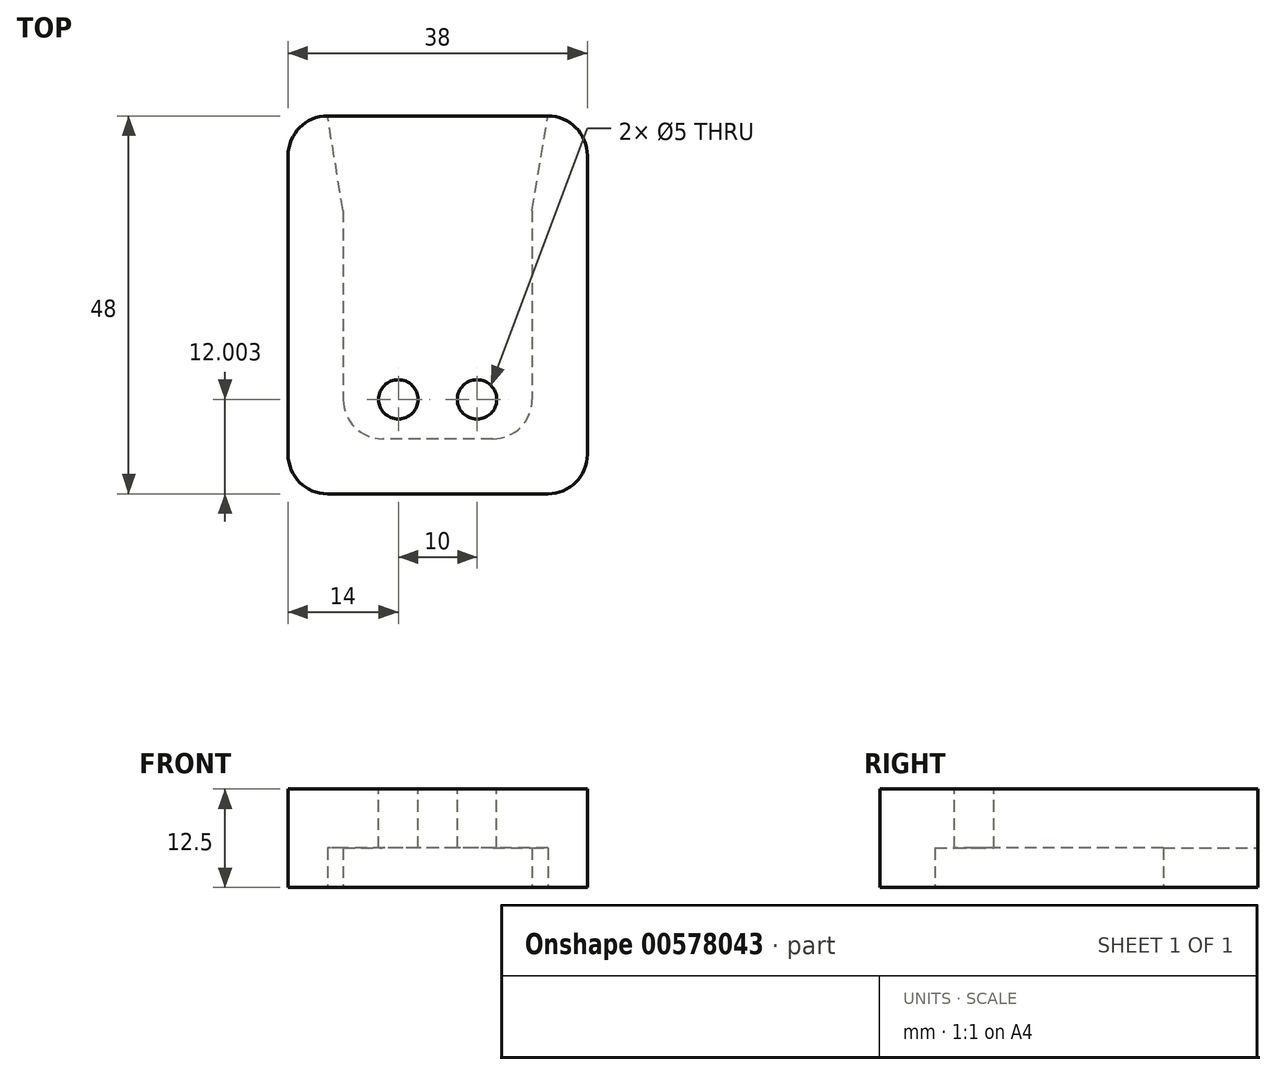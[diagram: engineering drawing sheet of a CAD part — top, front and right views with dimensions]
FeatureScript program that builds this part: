
annotation { "Feature Type Name" : "Feature", "Feature Type Description" : "" }
export const myFeature = defineFeature(function(context is Context, id is Id, definition is map)
    precondition{}
    {
        {
            var Q0;
            Q0=qCreatedBy(makeId("Top.planeOp"),FACE);
            var sketch = newSketch(context, id + "F0", { "sketchPlane" : qUnion([Q0])});
            skLineSegment(sketch, "E0.bottom", {"start": v(19, 24.01) * mm, "end": v(-19, 24.01) * mm});
            skLineSegment(sketch, "E0.top", {"start": v(19, -23.99) * mm, "end": v(-19, -23.99) * mm});
            skLineSegment(sketch, "E0.left", {"start": v(19, 24.01) * mm, "end": v(19, -23.99) * mm});
            skLineSegment(sketch, "E0.right", {"start": v(-19, 24.01) * mm, "end": v(-19, -23.99) * mm});
            skPoint(sketch, "E0.middle", {"position": v(0, 0.01) * mm});
            skLineSegment(sketch, "E1.bottom", {"start": v(12, 17.01) * mm, "end": v(-12, 17.01) * mm});
            skLineSegment(sketch, "E1.top", {"start": v(12, -16.99) * mm, "end": v(-12, -16.99) * mm});
            skLineSegment(sketch, "E1.left", {"start": v(12, 17.01) * mm, "end": v(12, -16.99) * mm});
            skLineSegment(sketch, "E1.right", {"start": v(-12, 17.01) * mm, "end": v(-12, -16.99) * mm});
            skSolve(sketch);
        }
        {
            var Q0;
            Q0=makeQuery(id+"F0.imprint","IMPRINT",FACE,{"disambiguationData":[TD([[makeQuery(id+"F0.imprint","IMPRINT",EDGE,{"derivedFrom":sQuery(id+"F0.wireOp",EDGE,"E0.bottom")}),1.0]])]});
            var Q1;
            Q1=makeQuery(id+"F0.imprint","IMPRINT",FACE,{"disambiguationData":[TD([[makeQuery(id+"F0.imprint","IMPRINT",EDGE,{"derivedFrom":sQuery(id+"F0.wireOp",EDGE,"E1.bottom")}),1.0]])]});
            extrude(context, id + "F1", {"entities" : qUnion([Q0, Q1]), "depth" : 12.5 * mm, "offsetDistance" : 25 * mm});
        }
        {
            var Q0;
            Q0=makeQuery(id+"F1.opExtrude","SWEPT_EDGE",EDGE,{"disambiguationData":[OSD([sQuery(id+"F0.wireOp",EDGE,"E0.top"),sQuery(id+"F0.wireOp",EDGE,"E0.right")])]});
            var Q1;
            Q1=makeQuery(id+"F1.opExtrude","SWEPT_EDGE",EDGE,{"disambiguationData":[OSD([sQuery(id+"F0.wireOp",EDGE,"E0.top"),sQuery(id+"F0.wireOp",EDGE,"E0.left")])]});
            var Q2;
            Q2=makeQuery(id+"F1.opExtrude","SWEPT_EDGE",EDGE,{"disambiguationData":[OSD([sQuery(id+"F0.wireOp",EDGE,"E0.bottom"),sQuery(id+"F0.wireOp",EDGE,"E0.left")])]});
            var Q3;
            Q3=makeQuery(id+"F1.opExtrude","SWEPT_EDGE",EDGE,{"disambiguationData":[OSD([sQuery(id+"F0.wireOp",EDGE,"E0.bottom"),sQuery(id+"F0.wireOp",EDGE,"E0.right")])]});
            fillet(context, id + "F2", {"entities" : qUnion([Q0, Q1, Q2, Q3]), "radius" : 5 * mm, "tangentPropagation" : true, "allowEdgeOverflow" : false});
        }
        {
            var Q0;
            Q0=makeQuery(id+"F1.opExtrude","CAP_FACE",FACE,{"disambiguationData":[OSD([sQuery(id+"F0.wireOp",EDGE,"E0.bottom"),sQuery(id+"F0.wireOp",EDGE,"E0.top"),sQuery(id+"F0.wireOp",EDGE,"E0.left"),sQuery(id+"F0.wireOp",EDGE,"E0.right")])],"isStart":false});
            var sketch = newSketch(context, id + "F3", { "sketchPlane" : qUnion([Q0])});
            skCircle(sketch, "E2", {"center": v(-5, -11.99) * mm, "radius": 2.5 * mm});
            skCircle(sketch, "E3", {"center": v(5, -11.99) * mm, "radius": 2.5 * mm});
            skLineSegment(sketch, "E4", {"start": v(-5, -11.99) * mm, "end": v(-19, -11.99) * mm, "construction": true});
            skLineSegment(sketch, "E5", {"start": v(5, -11.99) * mm, "end": v(19, -11.99) * mm, "construction": true});
            skLineSegment(sketch, "E6.bottom", {"start": v(-7.5, 24.01) * mm, "end": v(7.5, 24.01) * mm});
            skLineSegment(sketch, "E6.top", {"start": v(-7.5, 12.01) * mm, "end": v(7.5, 12.01) * mm});
            skLineSegment(sketch, "E6.left", {"start": v(-7.5, 24.01) * mm, "end": v(-7.5, 12.01) * mm});
            skLineSegment(sketch, "E6.right", {"start": v(7.5, 24.01) * mm, "end": v(7.5, 12.01) * mm});
            skLineSegment(sketch, "E7", {"start": v(-7.5, 14.34) * mm, "end": v(-19, 14.34) * mm, "construction": true});
            skLineSegment(sketch, "E8", {"start": v(7.5, 14.9) * mm, "end": v(19, 14.9) * mm, "construction": true});
            skSolve(sketch);
        }
        {
            var Q0;
            Q0=makeQuery(id+"F0.imprint","IMPRINT",FACE,{"disambiguationData":[TD([[makeQuery(id+"F0.imprint","IMPRINT",EDGE,{"derivedFrom":sQuery(id+"F0.wireOp",EDGE,"E1.bottom")}),1.0]])]});
            extrude(context, id + "F4", {"entities" : qUnion([Q0]), "operationType" : NewBodyOperationType.REMOVE, "depth" : 5 * mm, "offsetDistance" : 25 * mm});
        }
        {
            var Q0;
            Q0=makeQuery(id+"F4.boolean.opBoolean","COPY",EDGE,{"derivedFrom":makeQuery(id+"F4.opExtrude","SWEPT_EDGE",EDGE,{"disambiguationData":[OSD([sQuery(id+"F0.wireOp",EDGE,"E1.top"),sQuery(id+"F0.wireOp",EDGE,"E1.right")])]})});
            var Q1;
            Q1=makeQuery(id+"F4.boolean.opBoolean","COPY",EDGE,{"derivedFrom":makeQuery(id+"F4.opExtrude","SWEPT_EDGE",EDGE,{"disambiguationData":[OSD([sQuery(id+"F0.wireOp",EDGE,"E1.top"),sQuery(id+"F0.wireOp",EDGE,"E1.left")])]})});
            var Q2;
            Q2=makeQuery(id+"F4.boolean.opBoolean","COPY",EDGE,{"derivedFrom":makeQuery(id+"F4.opExtrude","SWEPT_EDGE",EDGE,{"disambiguationData":[OSD([sQuery(id+"F0.wireOp",EDGE,"E1.bottom"),sQuery(id+"F0.wireOp",EDGE,"E1.left")])]})});
            var Q3;
            Q3=makeQuery(id+"F4.boolean.opBoolean","COPY",EDGE,{"derivedFrom":makeQuery(id+"F4.opExtrude","SWEPT_EDGE",EDGE,{"disambiguationData":[OSD([sQuery(id+"F0.wireOp",EDGE,"E1.bottom"),sQuery(id+"F0.wireOp",EDGE,"E1.right")])]})});
            fillet(context, id + "F5", {"entities" : qUnion([Q0, Q1, Q2, Q3]), "radius" : 5 * mm, "tangentPropagation" : true, "allowEdgeOverflow" : false});
        }
        {
            var Q0;
            Q0=makeQuery(id+"F3.imprint","IMPRINT",FACE,{"disambiguationData":[TD([[makeQuery(id+"F3.imprint","IMPRINT",EDGE,{"derivedFrom":sQuery(id+"F3.wireOp",EDGE,"E2")}),1.0]])]});
            var Q1;
            Q1=makeQuery(id+"F3.imprint","IMPRINT",FACE,{"disambiguationData":[TD([[makeQuery(id+"F3.imprint","IMPRINT",EDGE,{"derivedFrom":sQuery(id+"F3.wireOp",EDGE,"E3")}),1.0]])]});
            extrude(context, id + "F6", {"entities" : qUnion([Q0, Q1]), "operationType" : NewBodyOperationType.REMOVE, "endBound" : BoundingType.UP_TO_NEXT, "oppositeDirection" : true, "depth" : 25 * mm, "offsetDistance" : 25 * mm});
        }
        {
            var Q0;
            Q0=makeQuery(id+"F1.opExtrude","CAP_FACE",FACE,{"disambiguationData":[OSD([sQuery(id+"F0.wireOp",EDGE,"E0.bottom"),sQuery(id+"F0.wireOp",EDGE,"E0.top"),sQuery(id+"F0.wireOp",EDGE,"E0.left"),sQuery(id+"F0.wireOp",EDGE,"E0.right")])],"isStart":true});
            var sketch = newSketch(context, id + "F7", { "sketchPlane" : qUnion([Q0])});
            skLineSegment(sketch, "E9", {"start": v(12, -12.01) * mm, "end": v(14, -24.01) * mm});
            skLineSegment(sketch, "E10", {"start": v(-12, -12.01) * mm, "end": v(-14, -24.01) * mm});
            skSolve(sketch);
        }
        {
            var Q0;
            Q0=makeQuery(id+"F7.imprint","IMPRINT",FACE,{"disambiguationData":[TD([[makeQuery(id+"F7.imprint","IMPRINT",EDGE,{"derivedFrom":sQuery(id+"F7.wireOp",EDGE,"E9")}),-1.0]])]});
            extrude(context, id + "F8", {"entities" : qUnion([Q0]), "operationType" : NewBodyOperationType.REMOVE, "oppositeDirection" : true, "depth" : 5 * mm, "offsetDistance" : 25 * mm});
        }
    });
